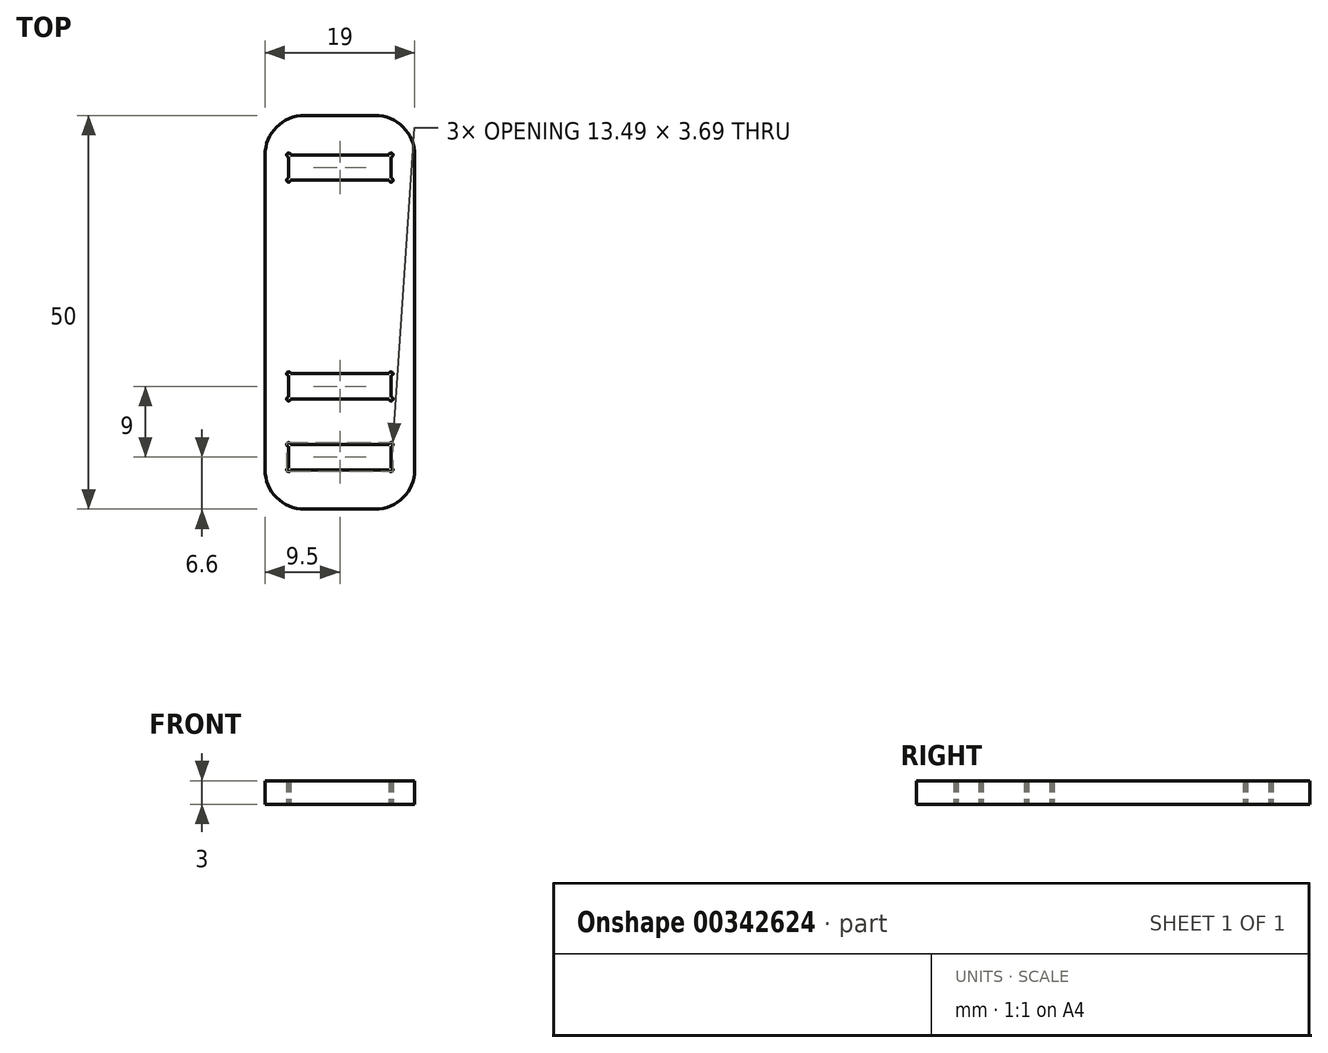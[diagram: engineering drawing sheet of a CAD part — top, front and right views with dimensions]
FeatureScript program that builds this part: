
annotation { "Feature Type Name" : "Feature", "Feature Type Description" : "" }
export const myFeature = defineFeature(function(context is Context, id is Id, definition is map)
    precondition{}
    {
        {
            var Q0;
            Q0=qCreatedBy(makeId("Top.planeOp"),FACE);
            var sketch = newSketch(context, id + "F0", { "sketchPlane" : qUnion([Q0])});
            skLineSegment(sketch, "E0.bottom", {"start": v(-4.5, 50) * mm, "end": v(4.5, 50) * mm});
            skLineSegment(sketch, "E0.top", {"start": v(-4.5, 0) * mm, "end": v(4.5, 0) * mm});
            skLineSegment(sketch, "E0.left", {"start": v(-9.5, 45) * mm, "end": v(-9.5, 5) * mm});
            skLineSegment(sketch, "E0.right", {"start": v(9.5, 45) * mm, "end": v(9.5, 5) * mm});
            skLineSegment(sketch, "E1.bottom", {"start": v(-6.5, 8.2) * mm, "end": v(6.5, 8.2) * mm});
            skLineSegment(sketch, "E1.top", {"start": v(-6.5, 5) * mm, "end": v(6.5, 5) * mm});
            skLineSegment(sketch, "E1.left", {"start": v(-6.5, 8.2) * mm, "end": v(-6.5, 5) * mm});
            skLineSegment(sketch, "E1.right", {"start": v(6.5, 8.2) * mm, "end": v(6.5, 5) * mm});
            skPoint(sketch, "E2", {"position": v(0, 5) * mm});
            skPoint(sketch, "E3", {"position": v(0, 0) * mm});
            skLineSegment(sketch, "E4", {"start": v(0, 5) * mm, "end": v(0, 0) * mm, "construction": true});
            skCircle(sketch, "E5", {"center": v(-6.5, 5) * mm, "radius": 0.25 * mm});
            skCircle(sketch, "E6", {"center": v(-6.5, 8.2) * mm, "radius": 0.25 * mm});
            skCircle(sketch, "E7.MirrorC", {"center": v(6.5, 5) * mm, "radius": 0.25 * mm});
            skCircle(sketch, "E8.MirrorC", {"center": v(6.5, 8.2) * mm, "radius": 0.25 * mm});
            skLineSegment(sketch, "E9", {"start": v(-9.5, 25) * mm, "end": v(9.5, 25) * mm, "construction": true});
            skLineSegment(sketch, "E10.MirrorCS", {"start": v(6.5, 5) * mm, "end": v(-6.5, 5) * mm});
            skLineSegment(sketch, "E11.MirrorCS", {"start": v(6.5, 8.2) * mm, "end": v(-6.5, 8.2) * mm});
            skLineSegment(sketch, "E12.MirrorCS", {"start": v(9.5, 25) * mm, "end": v(-9.5, 25) * mm, "construction": true});
            skCircle(sketch, "E13.MirrorC", {"center": v(-6.5, 45) * mm, "radius": 0.25 * mm});
            skLineSegment(sketch, "E14.MirrorCS", {"start": v(6.5, 45) * mm, "end": v(-6.5, 45) * mm});
            skCircle(sketch, "E15.MirrorC", {"center": v(-6.5, 41.8) * mm, "radius": 0.25 * mm});
            skLineSegment(sketch, "E16.MirrorCS", {"start": v(6.5, 41.8) * mm, "end": v(-6.5, 41.8) * mm});
            skCircle(sketch, "E17.MirrorC", {"center": v(6.5, 45) * mm, "radius": 0.25 * mm});
            skCircle(sketch, "E18.MirrorC", {"center": v(6.5, 41.8) * mm, "radius": 0.25 * mm});
            skLineSegment(sketch, "E19.MirrorCS", {"start": v(-6.5, 45) * mm, "end": v(6.5, 45) * mm});
            skLineSegment(sketch, "E20.MirrorCS", {"start": v(-6.5, 41.8) * mm, "end": v(6.5, 41.8) * mm});
            skLineSegment(sketch, "E21.MirrorCS", {"start": v(6.5, 41.8) * mm, "end": v(6.5, 45) * mm});
            skPoint(sketch, "E22.MirrorP", {"position": v(0, 45) * mm});
            skLineSegment(sketch, "E23.MirrorCS", {"start": v(-6.5, 41.8) * mm, "end": v(-6.5, 45) * mm});
            skPoint(sketch, "E24.visualSharp", {"position": v(-9.5, 50) * mm});
            skArc(sketch, "E24.filletArc", {"start": v(-4.5, 50) * mm, "mid": v(-8.04, 48.54) * mm, "end": v(-9.5, 45) * mm});
            skPoint(sketch, "E25.visualSharp", {"position": v(9.5, 50) * mm});
            skArc(sketch, "E25.filletArc", {"start": v(9.5, 45) * mm, "mid": v(8.04, 48.54) * mm, "end": v(4.5, 50) * mm});
            skPoint(sketch, "E26.visualSharp", {"position": v(9.5, 0) * mm});
            skArc(sketch, "E26.filletArc", {"start": v(4.5, 0) * mm, "mid": v(8.04, 1.46) * mm, "end": v(9.5, 5) * mm});
            skPoint(sketch, "E27.visualSharp", {"position": v(-9.5, 0) * mm});
            skArc(sketch, "E27.filletArc", {"start": v(-9.5, 5) * mm, "mid": v(-8.04, 1.46) * mm, "end": v(-4.5, 0) * mm});
            skLineSegment(sketch, "E28.0.1.0", {"start": v(-6.5, 17.2) * mm, "end": v(6.5, 17.2) * mm});
            skLineSegment(sketch, "E28.0.1.1", {"start": v(6.5, 17.2) * mm, "end": v(6.5, 14) * mm});
            skLineSegment(sketch, "E28.0.1.2", {"start": v(-6.5, 14) * mm, "end": v(6.5, 14) * mm});
            skPoint(sketch, "E28.0.1.3", {"position": v(0, 14) * mm});
            skLineSegment(sketch, "E28.0.1.4", {"start": v(-6.5, 17.2) * mm, "end": v(-6.5, 14) * mm});
            skLineSegment(sketch, "E28.0.1.5", {"start": v(-6.5, 17.2) * mm, "end": v(-6.5, 14) * mm});
            skLineSegment(sketch, "E28.0.1.6", {"start": v(6.5, 14) * mm, "end": v(-6.5, 14) * mm});
            skLineSegment(sketch, "E28.0.1.7", {"start": v(6.5, 17.2) * mm, "end": v(6.5, 14) * mm});
            skPoint(sketch, "E28.0.1.8", {"position": v(0, 14) * mm});
            skLineSegment(sketch, "E28.0.1.9", {"start": v(6.5, 17.2) * mm, "end": v(-6.5, 17.2) * mm});
            skLineSegment(sketch, "E28.0.1.10", {"start": v(-6.5, 17.2) * mm, "end": v(-6.5, 14) * mm});
            skPoint(sketch, "E28.0.1.11", {"position": v(0, 14) * mm});
            skLineSegment(sketch, "E28.0.1.12", {"start": v(6.5, 17.2) * mm, "end": v(6.5, 14) * mm});
            skLineSegment(sketch, "E28.0.1.13", {"start": v(-6.5, 14) * mm, "end": v(6.5, 14) * mm});
            skLineSegment(sketch, "E28.0.1.14", {"start": v(-6.5, 17.2) * mm, "end": v(6.5, 17.2) * mm});
            skLineSegment(sketch, "E28.0.1.15", {"start": v(6.5, 17.2) * mm, "end": v(6.5, 14) * mm});
            skLineSegment(sketch, "E28.0.1.16", {"start": v(-6.5, 17.2) * mm, "end": v(-6.5, 14) * mm});
            skLineSegment(sketch, "E28.0.1.17", {"start": v(6.5, 17.2) * mm, "end": v(-6.5, 17.2) * mm});
            skLineSegment(sketch, "E28.0.1.18", {"start": v(6.5, 14) * mm, "end": v(-6.5, 14) * mm});
            skPoint(sketch, "E28.0.1.19", {"position": v(0, 14) * mm});
            skCircle(sketch, "E28.0.1.20", {"center": v(6.5, 17.2) * mm, "radius": 0.25 * mm});
            skCircle(sketch, "E28.0.1.21", {"center": v(6.5, 14) * mm, "radius": 0.25 * mm});
            skCircle(sketch, "E28.0.1.22", {"center": v(-6.5, 14) * mm, "radius": 0.25 * mm});
            skCircle(sketch, "E28.0.1.23", {"center": v(-6.5, 17.2) * mm, "radius": 0.25 * mm});
            skCircle(sketch, "E28.0.1.24", {"center": v(-6.5, 14) * mm, "radius": 0.25 * mm});
            skCircle(sketch, "E28.0.1.25", {"center": v(6.5, 14) * mm, "radius": 0.25 * mm});
            skCircle(sketch, "E28.0.1.26", {"center": v(6.5, 17.2) * mm, "radius": 0.25 * mm});
            skCircle(sketch, "E28.0.1.27", {"center": v(-6.5, 17.2) * mm, "radius": 0.25 * mm});
            skCircle(sketch, "E28.0.1.28", {"center": v(-6.5, 14) * mm, "radius": 0.25 * mm});
            skCircle(sketch, "E28.0.1.29", {"center": v(6.5, 17.2) * mm, "radius": 0.25 * mm});
            skCircle(sketch, "E28.0.1.30", {"center": v(6.5, 14) * mm, "radius": 0.25 * mm});
            skCircle(sketch, "E28.0.1.31", {"center": v(-6.5, 17.2) * mm, "radius": 0.25 * mm});
            skCircle(sketch, "E28.0.1.32", {"center": v(6.5, 17.2) * mm, "radius": 0.25 * mm});
            skCircle(sketch, "E28.0.1.33", {"center": v(-6.5, 14) * mm, "radius": 0.25 * mm});
            skCircle(sketch, "E28.0.1.34", {"center": v(-6.5, 17.2) * mm, "radius": 0.25 * mm});
            skCircle(sketch, "E28.0.1.35", {"center": v(6.5, 14) * mm, "radius": 0.25 * mm});
            skLineSegment(sketch, "E28.direction1", {"start": v(-6.5, 5) * mm, "end": v(18, 5) * mm, "construction": true});
            skLineSegment(sketch, "E28.direction2", {"start": v(-6.5, 5) * mm, "end": v(-6.5, 14) * mm, "construction": true});
            skSolve(sketch);
        }
        {
            var Q0;
            Q0=makeQuery(id+"F0.imprint","IMPRINT",FACE,{"disambiguationData":[TD([[makeQuery(id+"F0.imprint","IMPRINT",EDGE,{"derivedFrom":sQuery(id+"F0.wireOp",EDGE,"E0.bottom")}),-1.0]])]});
            extrude(context, id + "F1", {"entities" : qUnion([Q0]), "depth" : 3 * mm});
        }
    });
